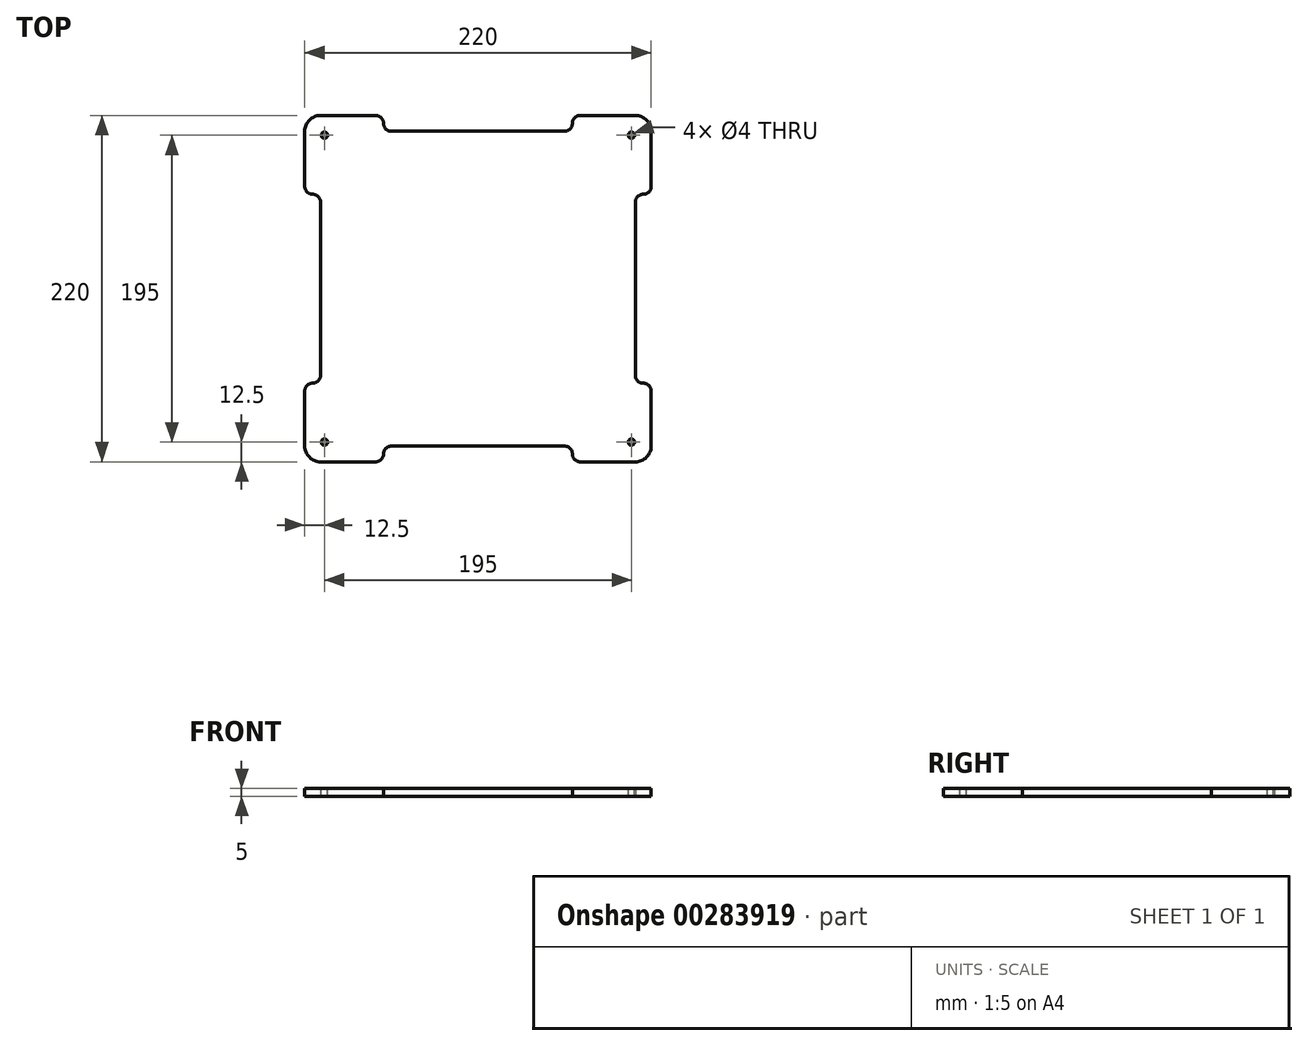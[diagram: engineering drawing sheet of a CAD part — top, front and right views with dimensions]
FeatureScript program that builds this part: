
annotation { "Feature Type Name" : "Feature", "Feature Type Description" : "" }
export const myFeature = defineFeature(function(context is Context, id is Id, definition is map)
    precondition{}
    {
        {
            var Q0;
            Q0=qCreatedBy(makeId("Top.planeOp"),FACE);
            var sketch = newSketch(context, id + "F0", { "sketchPlane" : qUnion([Q0])});
            skLineSegment(sketch, "E0.bottom", {"start": v(110, 110) * mm, "end": v(-110, 110) * mm});
            skLineSegment(sketch, "E0.top", {"start": v(110, -110) * mm, "end": v(-110, -110) * mm});
            skLineSegment(sketch, "E0.left", {"start": v(110, 110) * mm, "end": v(110, -110) * mm});
            skLineSegment(sketch, "E0.right", {"start": v(-110, 110) * mm, "end": v(-110, -110) * mm});
            skPoint(sketch, "E0.middle", {"position": v(0, 0) * mm});
            skSolve(sketch);
        }
        {
            var Q0;
            Q0 = qSketchRegion(id + "F0", true);
            extrude(context, id + "F1", {"entities" : qUnion([Q0]), "depth" : 5 * mm});
        }
        {
            var Q0;
            Q0=makeQuery(id+"F1.opExtrude","CAP_FACE",FACE,{"disambiguationData":[OSD([sQuery(id+"F0.wireOp",EDGE,"E0.bottom"),sQuery(id+"F0.wireOp",EDGE,"E0.top"),sQuery(id+"F0.wireOp",EDGE,"E0.left"),sQuery(id+"F0.wireOp",EDGE,"E0.right")])],"isStart":false});
            var sketch = newSketch(context, id + "F2", { "sketchPlane" : qUnion([Q0])});
            skCircle(sketch, "E1", {"center": v(-97.5, 97.5) * mm, "radius": 2 * mm});
            skCircle(sketch, "E2.1.0", {"center": v(-97.5, -97.5) * mm, "radius": 2 * mm});
            skCircle(sketch, "E2.2.0", {"center": v(97.5, -97.5) * mm, "radius": 2 * mm});
            skPoint(sketch, "E2.center", {"position": v(0, 0) * mm});
            skCircle(sketch, "E3.1.3.0", {"center": v(97.5, 97.5) * mm, "radius": 2 * mm});
            skSolve(sketch);
        }
        {
            var Q0;
            Q0 = qSketchRegion(id + "F2", true);
            extrude(context, id + "F3", {"entities" : qUnion([Q0]), "operationType" : NewBodyOperationType.REMOVE, "endBound" : BoundingType.THROUGH_ALL, "oppositeDirection" : true, "depth" : 25 * mm});
        }
        {
            var Q0;
            Q0=makeQuery(id+"F1.opExtrude","CAP_FACE",FACE,{"disambiguationData":[OSD([sQuery(id+"F0.wireOp",EDGE,"E0.bottom"),sQuery(id+"F0.wireOp",EDGE,"E0.top"),sQuery(id+"F0.wireOp",EDGE,"E0.left"),sQuery(id+"F0.wireOp",EDGE,"E0.right")])],"isStart":true});
            var sketch = newSketch(context, id + "F4", { "sketchPlane" : qUnion([Q0])});
            skLineSegment(sketch, "E4.bottom", {"start": v(100, 60) * mm, "end": v(120, 60) * mm});
            skLineSegment(sketch, "E4.top", {"start": v(100, -60) * mm, "end": v(120, -60) * mm});
            skLineSegment(sketch, "E4.left", {"start": v(100, 60) * mm, "end": v(100, -60) * mm});
            skLineSegment(sketch, "E4.right", {"start": v(120, 60) * mm, "end": v(120, -60) * mm});
            skPoint(sketch, "E4.middle", {"position": v(110, 0) * mm});
            skPoint(sketch, "E5.1.0", {"position": v(0, 110) * mm});
            skLineSegment(sketch, "E5.1.1", {"start": v(-60, 120) * mm, "end": v(60, 120) * mm});
            skLineSegment(sketch, "E5.1.2", {"start": v(-60, 100) * mm, "end": v(60, 100) * mm});
            skLineSegment(sketch, "E5.1.3", {"start": v(60, 100) * mm, "end": v(60, 120) * mm});
            skLineSegment(sketch, "E5.1.4", {"start": v(-60, 100) * mm, "end": v(-60, 120) * mm});
            skPoint(sketch, "E5.2.0", {"position": v(-110, 0) * mm});
            skLineSegment(sketch, "E5.2.1", {"start": v(-120, -60) * mm, "end": v(-120, 60) * mm});
            skLineSegment(sketch, "E5.2.2", {"start": v(-100, -60) * mm, "end": v(-100, 60) * mm});
            skLineSegment(sketch, "E5.2.3", {"start": v(-100, 60) * mm, "end": v(-120, 60) * mm});
            skLineSegment(sketch, "E5.2.4", {"start": v(-100, -60) * mm, "end": v(-120, -60) * mm});
            skPoint(sketch, "E5.center", {"position": v(0, 0) * mm});
            skLineSegment(sketch, "E6.1.3.0", {"start": v(60, -120) * mm, "end": v(-60, -120) * mm});
            skLineSegment(sketch, "E6.4.3.0", {"start": v(60, -100) * mm, "end": v(-60, -100) * mm});
            skPoint(sketch, "E6.6.3.0", {"position": v(0, -110) * mm});
            skLineSegment(sketch, "E6.7.3.0", {"start": v(-60, -100) * mm, "end": v(-60, -120) * mm});
            skLineSegment(sketch, "E6.10.3.0", {"start": v(60, -100) * mm, "end": v(60, -120) * mm});
            skSolve(sketch);
        }
        {
            var Q0;
            Q0 = qSketchRegion(id + "F4", true);
            extrude(context, id + "F5", {"entities" : qUnion([Q0]), "operationType" : NewBodyOperationType.REMOVE, "endBound" : BoundingType.THROUGH_ALL, "oppositeDirection" : true, "depth" : 25 * mm});
        }
        {
            var Q0;
            Q0=makeQuery(id+"F1.opExtrude","SWEPT_EDGE",EDGE,{"disambiguationData":[OSD([sQuery(id+"F0.wireOp",EDGE,"E0.top"),sQuery(id+"F0.wireOp",EDGE,"E0.left")])]});
            var Q1;
            Q1=makeQuery(id+"F1.opExtrude","SWEPT_EDGE",EDGE,{"disambiguationData":[OSD([sQuery(id+"F0.wireOp",EDGE,"E0.top"),sQuery(id+"F0.wireOp",EDGE,"E0.right")])]});
            var Q2;
            Q2=makeQuery(id+"F1.opExtrude","SWEPT_EDGE",EDGE,{"disambiguationData":[OSD([sQuery(id+"F0.wireOp",EDGE,"E0.bottom"),sQuery(id+"F0.wireOp",EDGE,"E0.left")])]});
            var Q3;
            Q3=makeQuery(id+"F1.opExtrude","SWEPT_EDGE",EDGE,{"disambiguationData":[OSD([sQuery(id+"F0.wireOp",EDGE,"E0.bottom"),sQuery(id+"F0.wireOp",EDGE,"E0.right")])]});
            fillet(context, id + "F6", {"entities" : qUnion([Q0, Q1, Q2, Q3]), "radius" : 10 * mm, "tangentPropagation" : true, "allowEdgeOverflow" : false});
        }
        {
            var Q0;
            Q0=makeQuery(id+"F5.boolean.opBoolean","INTERSECT",EDGE,{"derivedFrom":[makeQuery(id+"F1.opExtrude","SWEPT_FACE",FACE,{"disambiguationData":[OSD([sQuery(id+"F0.wireOp",EDGE,"E0.left")])]}),makeQuery(id+"F5.opExtrude","SWEPT_FACE",FACE,{"disambiguationData":[OSD([sQuery(id+"F4.wireOp",EDGE,"E4.top")])]})]});
            var Q1;
            Q1=makeQuery(id+"F5.boolean.opBoolean","COPY",EDGE,{"derivedFrom":makeQuery(id+"F5.opExtrude","SWEPT_EDGE",EDGE,{"disambiguationData":[OSD([sQuery(id+"F4.wireOp",EDGE,"E4.top"),sQuery(id+"F4.wireOp",EDGE,"E4.left")])]})});
            var Q2;
            Q2=makeQuery(id+"F5.boolean.opBoolean","COPY",EDGE,{"derivedFrom":makeQuery(id+"F5.opExtrude","SWEPT_EDGE",EDGE,{"disambiguationData":[OSD([sQuery(id+"F4.wireOp",EDGE,"E4.bottom"),sQuery(id+"F4.wireOp",EDGE,"E4.left")])]})});
            var Q3;
            Q3=makeQuery(id+"F5.boolean.opBoolean","INTERSECT",EDGE,{"derivedFrom":[makeQuery(id+"F1.opExtrude","SWEPT_FACE",FACE,{"disambiguationData":[OSD([sQuery(id+"F0.wireOp",EDGE,"E0.left")])]}),makeQuery(id+"F5.opExtrude","SWEPT_FACE",FACE,{"disambiguationData":[OSD([sQuery(id+"F4.wireOp",EDGE,"E4.bottom")])]})]});
            var Q4;
            Q4=makeQuery(id+"F5.boolean.opBoolean","COPY",EDGE,{"derivedFrom":makeQuery(id+"F5.opExtrude","SWEPT_EDGE",EDGE,{"disambiguationData":[OSD([sQuery(id+"F4.wireOp",EDGE,"E5.1.2"),sQuery(id+"F4.wireOp",EDGE,"E5.1.3")])]})});
            var Q5;
            Q5=makeQuery(id+"F5.boolean.opBoolean","INTERSECT",EDGE,{"derivedFrom":[makeQuery(id+"F1.opExtrude","SWEPT_FACE",FACE,{"disambiguationData":[OSD([sQuery(id+"F0.wireOp",EDGE,"E0.top")])]}),makeQuery(id+"F5.opExtrude","SWEPT_FACE",FACE,{"disambiguationData":[OSD([sQuery(id+"F4.wireOp",EDGE,"E5.1.3")])]})]});
            var Q6;
            Q6=makeQuery(id+"F5.boolean.opBoolean","COPY",EDGE,{"derivedFrom":makeQuery(id+"F5.opExtrude","SWEPT_EDGE",EDGE,{"disambiguationData":[OSD([sQuery(id+"F4.wireOp",EDGE,"E5.1.2"),sQuery(id+"F4.wireOp",EDGE,"E5.1.4")])]})});
            var Q7;
            Q7=makeQuery(id+"F5.boolean.opBoolean","INTERSECT",EDGE,{"derivedFrom":[makeQuery(id+"F1.opExtrude","SWEPT_FACE",FACE,{"disambiguationData":[OSD([sQuery(id+"F0.wireOp",EDGE,"E0.top")])]}),makeQuery(id+"F5.opExtrude","SWEPT_FACE",FACE,{"disambiguationData":[OSD([sQuery(id+"F4.wireOp",EDGE,"E5.1.4")])]})]});
            var Q8;
            Q8=makeQuery(id+"F5.boolean.opBoolean","COPY",EDGE,{"derivedFrom":makeQuery(id+"F5.opExtrude","SWEPT_EDGE",EDGE,{"disambiguationData":[OSD([sQuery(id+"F4.wireOp",EDGE,"E5.2.2"),sQuery(id+"F4.wireOp",EDGE,"E5.2.3")])]})});
            var Q9;
            Q9=makeQuery(id+"F5.boolean.opBoolean","INTERSECT",EDGE,{"derivedFrom":[makeQuery(id+"F1.opExtrude","SWEPT_FACE",FACE,{"disambiguationData":[OSD([sQuery(id+"F0.wireOp",EDGE,"E0.right")])]}),makeQuery(id+"F5.opExtrude","SWEPT_FACE",FACE,{"disambiguationData":[OSD([sQuery(id+"F4.wireOp",EDGE,"E5.2.3")])]})]});
            var Q10;
            Q10=makeQuery(id+"F5.boolean.opBoolean","COPY",EDGE,{"derivedFrom":makeQuery(id+"F5.opExtrude","SWEPT_EDGE",EDGE,{"disambiguationData":[OSD([sQuery(id+"F4.wireOp",EDGE,"E5.2.2"),sQuery(id+"F4.wireOp",EDGE,"E5.2.4")])]})});
            var Q11;
            Q11=makeQuery(id+"F5.boolean.opBoolean","INTERSECT",EDGE,{"derivedFrom":[makeQuery(id+"F1.opExtrude","SWEPT_FACE",FACE,{"disambiguationData":[OSD([sQuery(id+"F0.wireOp",EDGE,"E0.right")])]}),makeQuery(id+"F5.opExtrude","SWEPT_FACE",FACE,{"disambiguationData":[OSD([sQuery(id+"F4.wireOp",EDGE,"E5.2.4")])]})]});
            var Q12;
            Q12=makeQuery(id+"F5.boolean.opBoolean","COPY",EDGE,{"derivedFrom":makeQuery(id+"F5.opExtrude","SWEPT_EDGE",EDGE,{"disambiguationData":[OSD([sQuery(id+"F4.wireOp",EDGE,"E6.4.3.0"),sQuery(id+"F4.wireOp",EDGE,"E6.7.3.0")])]})});
            var Q13;
            Q13=makeQuery(id+"F5.boolean.opBoolean","INTERSECT",EDGE,{"derivedFrom":[makeQuery(id+"F1.opExtrude","SWEPT_FACE",FACE,{"disambiguationData":[OSD([sQuery(id+"F0.wireOp",EDGE,"E0.bottom")])]}),makeQuery(id+"F5.opExtrude","SWEPT_FACE",FACE,{"disambiguationData":[OSD([sQuery(id+"F4.wireOp",EDGE,"E6.7.3.0")])]})]});
            var Q14;
            Q14=makeQuery(id+"F5.boolean.opBoolean","COPY",EDGE,{"derivedFrom":makeQuery(id+"F5.opExtrude","SWEPT_EDGE",EDGE,{"disambiguationData":[OSD([sQuery(id+"F4.wireOp",EDGE,"E6.4.3.0"),sQuery(id+"F4.wireOp",EDGE,"E6.10.3.0")])]})});
            var Q15;
            Q15=makeQuery(id+"F5.boolean.opBoolean","INTERSECT",EDGE,{"derivedFrom":[makeQuery(id+"F1.opExtrude","SWEPT_FACE",FACE,{"disambiguationData":[OSD([sQuery(id+"F0.wireOp",EDGE,"E0.bottom")])]}),makeQuery(id+"F5.opExtrude","SWEPT_FACE",FACE,{"disambiguationData":[OSD([sQuery(id+"F4.wireOp",EDGE,"E6.10.3.0")])]})]});
            fillet(context, id + "F7", {"entities" : qUnion([Q0, Q1, Q2, Q3, Q4, Q5, Q6, Q7, Q8, Q9, Q10, Q11, Q12, Q13, Q14, Q15]), "radius" : 5 * mm, "tangentPropagation" : true, "allowEdgeOverflow" : false});
        }
    });
